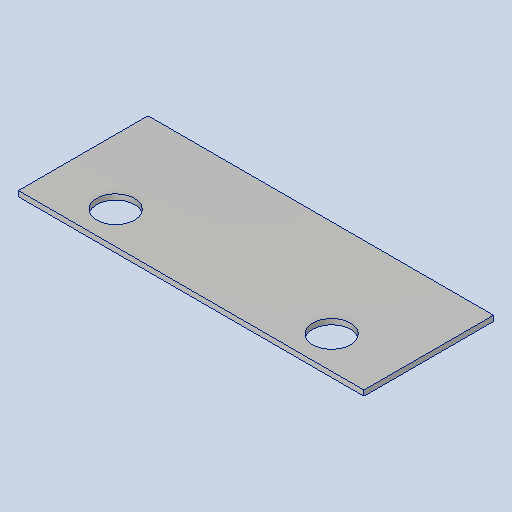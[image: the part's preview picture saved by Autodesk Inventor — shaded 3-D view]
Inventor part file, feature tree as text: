
AUTODESK INVENTOR PART (.ipt)
format: ipt  version: 2023.4 (Build 274418000, 418)  size: 90,624 bytes
history: native  units: in
note: dims shown in document units (in); Inventor stores cm internally (conversion verified against a paired STEP export)
features: other x3, sketch x2
ambient origin geometry x8: Origin, YZ Plane, XZ Plane, XY Plane, X Axis, Y Axis, Z Axis, Center Point
bodies: Solid1 (feature_tree)
feature tree (5):
  other  "GP2-002.ipt"
  other  "Solid1::GP2-002.ipt"
  other  "TaggingFeature1"
  sketch  "Sketch1"  dims[d0=0.3937in]
  sketch  "Sketch2"
